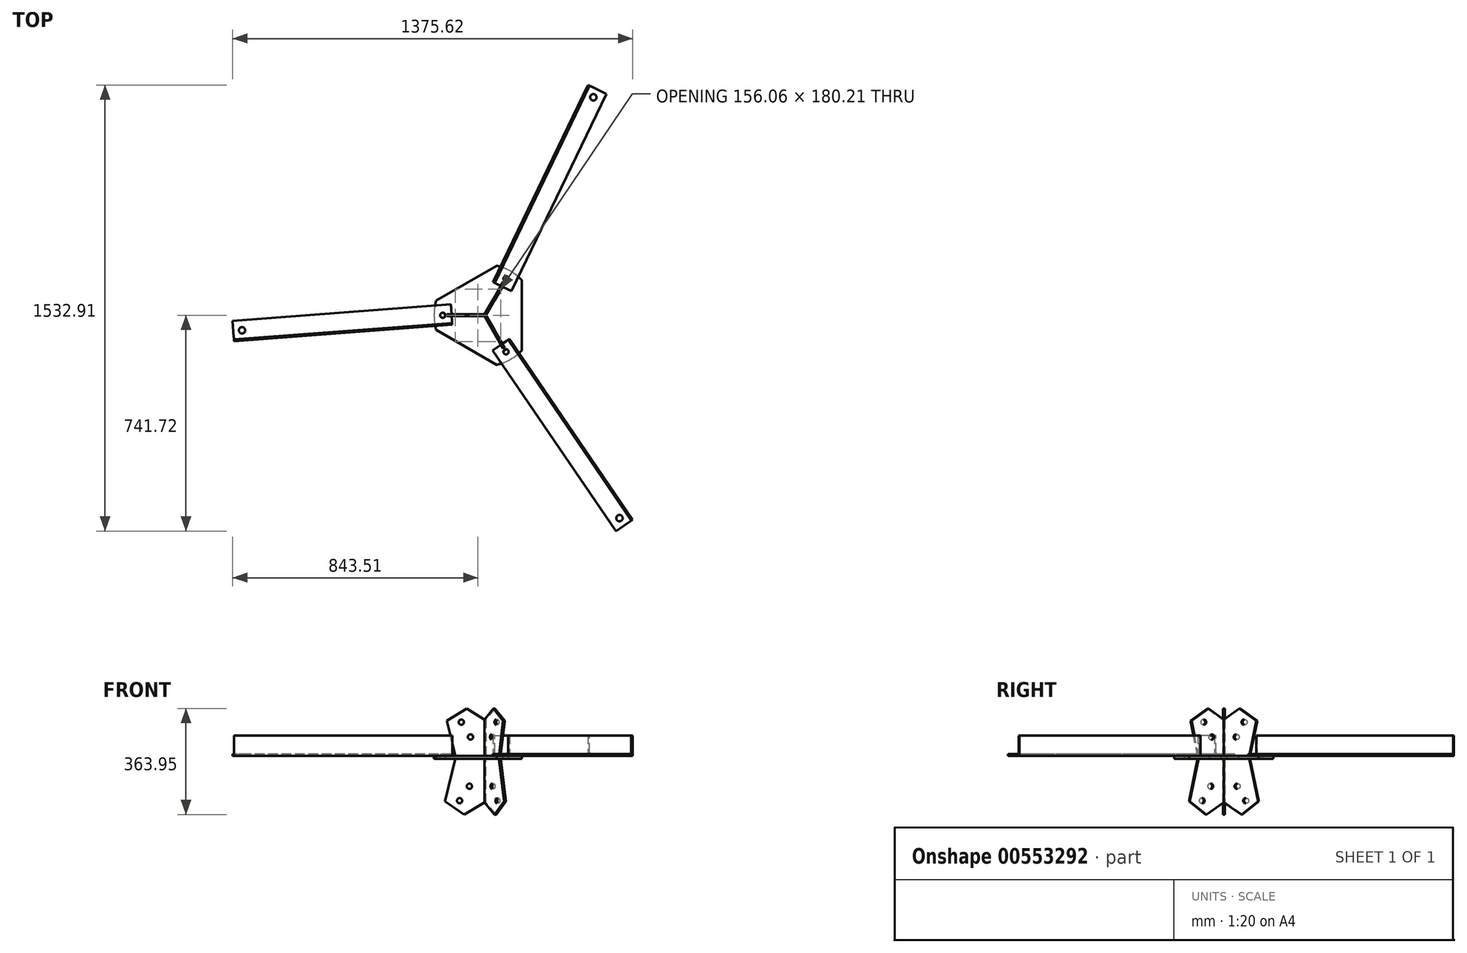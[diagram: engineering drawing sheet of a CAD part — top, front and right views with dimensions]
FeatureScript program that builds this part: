
annotation { "Feature Type Name" : "Feature", "Feature Type Description" : "" }
export const myFeature = defineFeature(function(context is Context, id is Id, definition is map)
    precondition{}
    {
        {
            var Q0;
            Q0=qCreatedBy(makeId("Top.planeOp"),FACE);
            var sketch = newSketch(context, id + "F0", { "sketchPlane" : qUnion([Q0])});
            skArc(sketch, "E0", {"start": v(40.55, -170.24) * mm, "mid": v(87.5, -151.55) * mm, "end": v(127.15, -120.24) * mm});
            skLineSegment(sketch, "E1", {"start": v(40.55, -170.24) * mm, "end": v(-167.7, -50) * mm});
            skLineSegment(sketch, "E2", {"start": v(0, 0) * mm, "end": v(-248.61, 0) * mm, "construction": true});
            skLineSegment(sketch, "E3.MirrorCS", {"start": v(40.55, 170.24) * mm, "end": v(-167.7, 50) * mm});
            skLineSegment(sketch, "E4", {"start": v(0, 0) * mm, "end": v(113.61, -196.78) * mm, "construction": true});
            skLineSegment(sketch, "E5.MirrorCS", {"start": v(127.15, -120.24) * mm, "end": v(127.15, 120.24) * mm});
            skArc(sketch, "E6.trimOffspring", {"start": v(-167.7, 50) * mm, "mid": v(-175, 0) * mm, "end": v(-167.7, -50) * mm});
            skArc(sketch, "E7.trimOffspring", {"start": v(127.15, 120.24) * mm, "mid": v(87.5, 151.55) * mm, "end": v(40.55, 170.24) * mm});
            skSolve(sketch);
        }
        {
            var Q0;
            Q0=makeQuery(id+"F0.imprint","IMPRINT",FACE,{"disambiguationData":[TD([[makeQuery(id+"F0.imprint","IMPRINT",EDGE,{"derivedFrom":sQuery(id+"F0.wireOp",EDGE,"E0")}),1.0]])]});
            extrude(context, id + "F1", {"entities" : qUnion([Q0]), "depth" : 10 * mm, "offsetDistance" : 25 * mm});
        }
        {
            var Q0;
            Q0=makeQuery(id+"F1.opExtrude","CAP_FACE",FACE,{"disambiguationData":[OSD([sQuery(id+"F0.wireOp",EDGE,"E0"),sQuery(id+"F0.wireOp",EDGE,"oJbW3ULZ-2pRP-CatU-Atqn-FDPEkCRfx0l3")])],"isStart":false});
            var sketch = newSketch(context, id + "F2", { "sketchPlane" : qUnion([Q0])});
            skCircle(sketch, "E8", {"center": v(-145, 0) * mm, "radius": 9 * mm});
            skCircle(sketch, "E9", {"center": v(72.5, -125.57) * mm, "radius": 9 * mm});
            skCircle(sketch, "E10", {"center": v(72.5, 125.57) * mm, "radius": 9 * mm});
            skCircle(sketch, "E11", {"center": v(0, 0) * mm, "radius": 145 * mm, "construction": true});
            skLineSegment(sketch, "E12", {"start": v(72.5, 125.57) * mm, "end": v(0, 0) * mm});
            skLineSegment(sketch, "E13", {"start": v(0, 0) * mm, "end": v(-145, 0) * mm});
            skLineSegment(sketch, "E14", {"start": v(0, 0) * mm, "end": v(72.5, -125.57) * mm});
            skSolve(sketch);
        }
        {
            var Q0;
            Q0 = qSketchRegion(id + "F2", true);
            extrude(context, id + "F3", {"entities" : qUnion([Q0]), "operationType" : NewBodyOperationType.REMOVE, "oppositeDirection" : true, "depth" : 25 * mm, "offsetDistance" : 25 * mm});
        }
        {
            var Q0;
            Q0=makeQuery(id+"F1.opExtrude","CAP_FACE",FACE,{"disambiguationData":[OSD([sQuery(id+"F0.wireOp",EDGE,"E0")])],"isStart":false});
            var sketch = newSketch(context, id + "F4", { "sketchPlane" : qUnion([Q0])});
            skLineSegment(sketch, "E15", {"start": v(0, 0) * mm, "end": v(72.5, -125.57) * mm, "construction": true});
            skLineSegment(sketch, "E16", {"start": v(0, 0) * mm, "end": v(-145, 0) * mm, "construction": true});
            skLineSegment(sketch, "E17", {"start": v(0, 0) * mm, "end": v(72.5, 125.57) * mm, "construction": true});
            skLineSegment(sketch, "E18.0", {"start": v(-2.02, 3.5) * mm, "end": v(-74.92, 3.5) * mm});
            skLineSegment(sketch, "E18.1", {"start": v(-2.02, 3.5) * mm, "end": v(34.43, 66.63) * mm});
            skLineSegment(sketch, "E19.0", {"start": v(-2.02, -3.5) * mm, "end": v(-74.92, -3.5) * mm});
            skLineSegment(sketch, "E19.1", {"start": v(-2.02, -3.5) * mm, "end": v(34.47, -66.7) * mm});
            skLineSegment(sketch, "E20.0", {"start": v(4.04, 0) * mm, "end": v(40.53, -63.2) * mm});
            skLineSegment(sketch, "E20.1", {"start": v(4.04, 0) * mm, "end": v(40.5, 63.13) * mm});
            skLineSegment(sketch, "E21", {"start": v(40.53, -63.2) * mm, "end": v(34.47, -66.7) * mm});
            skLineSegment(sketch, "E22", {"start": v(40.5, 63.13) * mm, "end": v(34.43, 66.63) * mm});
            skCircle(sketch, "E23", {"center": v(0, 0) * mm, "radius": 75 * mm, "construction": true});
            skLineSegment(sketch, "E24", {"start": v(-74.92, -3.5) * mm, "end": v(-74.92, 3.5) * mm});
            skSolve(sketch);
        }
        {
            var Q0;
            Q0=qCreatedBy(makeId("Front.planeOp"),FACE);
            var sketch = newSketch(context, id + "F5", { "sketchPlane" : qUnion([Q0])});
            skLineSegment(sketch, "E25.trimOffspring", {"start": v(0, -16) * mm, "end": v(-925, -1374.5) * mm, "construction": true});
            skLineSegment(sketch, "E26", {"start": v(0, 0) * mm, "end": v(0, -32) * mm, "construction": true});
            skLineSegment(sketch, "E27", {"start": v(0, -16) * mm, "end": v(-196.24, -16) * mm, "construction": true});
            skLineSegment(sketch, "E28", {"start": v(-133.05, -149.22) * mm, "end": v(-65.51, -50.03) * mm, "construction": true});
            skLineSegment(sketch, "E29", {"start": v(-65.51, -50.03) * mm, "end": v(-7.65, -89.43) * mm, "construction": true});
            skLineSegment(sketch, "E30", {"start": v(-7.65, -89.43) * mm, "end": v(-75.2, -188.62) * mm, "construction": true});
            skCircle(sketch, "E31", {"center": v(-53.47, -94.53) * mm, "radius": 9 * mm});
            skCircle(sketch, "E32", {"center": v(-87.24, -144.12) * mm, "radius": 9 * mm});
            skLineSegment(sketch, "E33", {"start": v(-133.05, -149.22) * mm, "end": v(-75.2, -188.62) * mm, "construction": true});
            skLineSegment(sketch, "E34", {"start": v(-2.02, 0) * mm, "end": v(-102.02, 0) * mm});
            skLineSegment(sketch, "E35", {"start": v(-102.02, 0) * mm, "end": v(-137.18, -146.4) * mm});
            skLineSegment(sketch, "E36", {"start": v(-137.18, -146.4) * mm, "end": v(-71.06, -191.43) * mm});
            skLineSegment(sketch, "E37", {"start": v(-71.06, -191.43) * mm, "end": v(-2.02, -150) * mm});
            skLineSegment(sketch, "E38", {"start": v(-2.02, -150) * mm, "end": v(-2.02, 0) * mm});
            skSolve(sketch);
        }
        {
            var Q0;
            Q0 = qSketchRegion(id + "F5", true);
            extrude(context, id + "F6", {"entities" : qUnion([Q0]), "depth" : 7 * mm, "offsetDistance" : 25 * mm, "symmetric" : true});
        }
        {
            var Q0;
            Q0=makeQuery(id+"F6.opExtrude","SWEPT_BODY",BODY,{"disambiguationData":[OSD([sQuery(id+"F5.wireOp",EDGE,"E31"),sQuery(id+"F5.wireOp",EDGE,"E32"),sQuery(id+"F5.wireOp",EDGE,"E34"),sQuery(id+"F5.wireOp",EDGE,"E35"),sQuery(id+"F5.wireOp",EDGE,"E36"),sQuery(id+"F5.wireOp",EDGE,"E37"),sQuery(id+"F5.wireOp",EDGE,"E38")])]});
            var Q1;
            Q1=sQuery(id+"F4.wireOp",EDGE,"E23");
            circularPattern(context, id + "F7", {"entities" : qUnion([Q0]), "axis" : qUnion([Q1]), "angle" : 360 * degree, "instanceCount" : 3, "equalSpace" : true, "computeTransformsWithoutBuiltin" : true});
        }
        {
            var Q0;
            Q0=makeQuery(id+"F4.imprint","IMPRINT",FACE,{"disambiguationData":[TD([[makeQuery(id+"F4.imprint","IMPRINT",EDGE,{"derivedFrom":sQuery(id+"F4.wireOp",EDGE,"E18.0")}),1.0]])]});
            var sketch = newSketch(context, id + "F8", { "sketchPlane" : qUnion([Q0])});
            skLineSegment(sketch, "E39", {"start": v(-2.02, 3.5) * mm, "end": v(4.04, 0) * mm});
            skLineSegment(sketch, "E40", {"start": v(4.04, 0) * mm, "end": v(-2.02, -3.5) * mm});
            skLineSegment(sketch, "E41", {"start": v(-2.02, -3.5) * mm, "end": v(-2.02, 3.5) * mm});
            skSolve(sketch);
        }
        {
            var Q0;
            Q0 = qSketchRegion(id + "F8", true);
            var Q1;
            Q1=makeQuery(id+"F6.opExtrude","CAP_VERTEX",VERTEX,{"disambiguationData":[OSD([sQuery(id+"F5.wireOp",EDGE,"E37"),sQuery(id+"F5.wireOp",EDGE,"E38")])],"isStart":true});
            extrude(context, id + "F9", {"entities" : qUnion([Q0]), "operationType" : NewBodyOperationType.ADD, "endBound" : BoundingType.UP_TO_VERTEX, "oppositeDirection" : true, "depth" : 200 * mm, "endBoundEntityVertex" : qUnion([Q1]), "offsetDistance" : 25 * mm});
        }
        {
            var Q0;
            Q0=makeQuery(id+"F2.imprint","IMPRINT",FACE,{"disambiguationData":[TD([[makeQuery(id+"F2.imprint","IMPRINT",EDGE,{"derivedFrom":sQuery(id+"F2.wireOp",EDGE,"E8")}),-1.0]])]});
            var sketch = newSketch(context, id + "F10", { "sketchPlane" : qUnion([Q0])});
            skLineSegment(sketch, "E42", {"start": v(-115.08, 2.24) * mm, "end": v(-864.88, -54) * mm});
            skLineSegment(sketch, "E43", {"start": v(-145, 0) * mm, "end": v(-838.84, 0) * mm, "construction": true});
            skLineSegment(sketch, "E44", {"start": v(-838.84, 0) * mm, "end": v(-838.84, 0) * mm});
            skLineSegment(sketch, "E45", {"start": v(-838.84, 0) * mm, "end": v(-834.96, -51.75) * mm, "construction": true});
            skSolve(sketch);
        }
        {
            var Q0;
            Q0=sQuery(id+"F10.wireOp",VERTEX,"E42.start");
            var Q1;
            Q1=sQuery(id+"F10.wireOp",EDGE,"E42");
            cPlane(context, id + "F11", {"entities" : qUnion([Q0, Q1]), "cplaneType" : CPlaneType.LINE_POINT, "offset" : 25 * mm, "width" : 150 * mm, "height" : 150 * mm});
        }
        {
            var Q0;
            Q0=qCreatedBy(id+"F11.planeOp",FACE);
            var sketch = newSketch(context, id + "F12", { "sketchPlane" : qUnion([Q0])});
            skLineSegment(sketch, "E46", {"start": v(24.15, 10) * mm, "end": v(-45.85, 10) * mm});
            skLineSegment(sketch, "E47", {"start": v(-45.85, 10) * mm, "end": v(-45.85, 16) * mm});
            skLineSegment(sketch, "E48", {"start": v(-45.85, 16) * mm, "end": v(10.15, 16) * mm});
            skLineSegment(sketch, "E49", {"start": v(18.15, 24) * mm, "end": v(18.15, 80) * mm});
            skLineSegment(sketch, "E50", {"start": v(18.15, 80) * mm, "end": v(24.15, 80) * mm});
            skLineSegment(sketch, "E51", {"start": v(24.15, 80) * mm, "end": v(24.15, 10) * mm});
            skPoint(sketch, "E52.visualSharp", {"position": v(18.15, 16) * mm});
            skArc(sketch, "E52.filletArc", {"start": v(10.15, 16) * mm, "mid": v(15.81, 18.34) * mm, "end": v(18.15, 24) * mm});
            skSolve(sketch);
        }
        {
            var Q0;
            Q0 = qSketchRegion(id + "F12", true);
            var Q1;
            Q1=sQuery(id+"F10.wireOp",EDGE,"E42");
            sweep(context, id + "F13", {"profiles" : qUnion([Q0]), "path" : qUnion([Q1])});
        }
        {
            var Q0;
            Q0=makeQuery(id+"F13.opSweep","SWEPT_FACE",FACE,{"disambiguationData":[OSD([sQuery(id+"F10.wireOp",EDGE,"E42"),sQuery(id+"F12.wireOp",EDGE,"E48")])]});
            var sketch = newSketch(context, id + "F14", { "sketchPlane" : qUnion([Q0])});
            skCircle(sketch, "E53.0", {"center": v(-145, 0) * mm, "radius": 9 * mm});
            skLineSegment(sketch, "E54", {"start": v(-492.6, 9.02) * mm, "end": v(-492.64, 9.59) * mm, "construction": true});
            skCircle(sketch, "E55.MirrorC", {"center": v(-834.96, -51.75) * mm, "radius": 9 * mm, "construction": true});
            skCircle(sketch, "E56", {"center": v(-834.96, -51.75) * mm, "radius": 11 * mm});
            skSolve(sketch);
        }
        {
            var Q0;
            Q0=sQuery(id+"F14.wireOp",VERTEX,"E53.0.center");
            var Q1;
            Q1=makeQuery(id+"F13.opSweep","SWEPT_BODY",BODY,{"disambiguationData":[OSD([sQuery(id+"F10.wireOp",EDGE,"E42"),sQuery(id+"F12.wireOp",EDGE,"E46"),sQuery(id+"F12.wireOp",EDGE,"E47"),sQuery(id+"F12.wireOp",EDGE,"E48"),sQuery(id+"F12.wireOp",EDGE,"E49"),sQuery(id+"F12.wireOp",EDGE,"E50"),sQuery(id+"F12.wireOp",EDGE,"E51"),sQuery(id+"F12.wireOp",EDGE,"E52.filletArc")])]});
            hole(context, id + "F15", {"style" : HoleStyle.SIMPLE, "endStyle" : HoleEndStyle.BLIND, "holeDiameter" : 18 * mm, "majorDiameter" : 5 * mm, "holeDepth" : 22 * mm, "isTappedThrough" : true, "tappedDepth" : 12 * mm, "tapClearance" : 3, "locations" : qUnion([Q0]), "scope" : qUnion([Q1]), "startStyle" : HoleStartStyle.PART});
        }
        {
            var Q0;
            Q0=sQuery(id+"F10.wireOp",VERTEX,"E45.end");
            var Q1;
            Q1=makeQuery(id+"F13.opSweep","SWEPT_BODY",BODY,{"disambiguationData":[OSD([sQuery(id+"F10.wireOp",EDGE,"E42"),sQuery(id+"F12.wireOp",EDGE,"E46"),sQuery(id+"F12.wireOp",EDGE,"E47"),sQuery(id+"F12.wireOp",EDGE,"E48"),sQuery(id+"F12.wireOp",EDGE,"E49"),sQuery(id+"F12.wireOp",EDGE,"E50"),sQuery(id+"F12.wireOp",EDGE,"E51"),sQuery(id+"F12.wireOp",EDGE,"E52.filletArc")])]});
            hole(context, id + "F16", {"style" : HoleStyle.SIMPLE, "endStyle" : HoleEndStyle.BLIND, "oppositeDirection" : true, "holeDiameter" : 22 * mm, "majorDiameter" : 5 * mm, "holeDepth" : 22 * mm, "isTappedThrough" : true, "tappedDepth" : 12 * mm, "tapClearance" : 3, "locations" : qUnion([Q0]), "scope" : qUnion([Q1]), "startStyle" : HoleStartStyle.PART});
        }
        {
            var Q0;
            Q0=makeQuery(id+"F13.opSweep","SWEPT_BODY",BODY,{"disambiguationData":[OSD([sQuery(id+"F10.wireOp",EDGE,"E42"),sQuery(id+"F12.wireOp",EDGE,"E46"),sQuery(id+"F12.wireOp",EDGE,"E47"),sQuery(id+"F12.wireOp",EDGE,"E48"),sQuery(id+"F12.wireOp",EDGE,"E49"),sQuery(id+"F12.wireOp",EDGE,"E50"),sQuery(id+"F12.wireOp",EDGE,"E51"),sQuery(id+"F12.wireOp",EDGE,"E52.filletArc")])]});
            var Q1;
            Q1=sQuery(id+"F4.wireOp",EDGE,"E23");
            circularPattern(context, id + "F17", {"entities" : qUnion([Q0]), "axis" : qUnion([Q1]), "angle" : 360 * degree, "instanceCount" : 3, "equalSpace" : true, "computeTransformsWithoutBuiltin" : true});
        }
        {
            var Q0;
            Q0=qCreatedBy(makeId("Front.planeOp"),FACE);
            var sketch = newSketch(context, id + "F18", { "sketchPlane" : qUnion([Q0])});
            skLineSegment(sketch, "E57", {"start": v(-2.02, 10) * mm, "end": v(-102.02, 10) * mm});
            skLineSegment(sketch, "E58", {"start": v(-102.02, 10) * mm, "end": v(-130.9, 130.66) * mm});
            skLineSegment(sketch, "E59", {"start": v(-130.9, 130.66) * mm, "end": v(-62.74, 172.52) * mm});
            skLineSegment(sketch, "E60", {"start": v(-62.74, 172.52) * mm, "end": v(-2.02, 135) * mm});
            skLineSegment(sketch, "E61", {"start": v(-2.02, 135) * mm, "end": v(-2.02, 10) * mm});
            skLineSegment(sketch, "E62", {"start": v(-3.72, 0) * mm, "end": v(-925, 1500) * mm, "construction": true});
            skLineSegment(sketch, "E63", {"start": v(-126.65, 133.27) * mm, "end": v(-63.85, 31.02) * mm, "construction": true});
            skLineSegment(sketch, "E64", {"start": v(-63.85, 31.02) * mm, "end": v(-4.2, 67.65) * mm, "construction": true});
            skLineSegment(sketch, "E65", {"start": v(-4.2, 67.65) * mm, "end": v(-67, 169.9) * mm, "construction": true});
            skLineSegment(sketch, "E66", {"start": v(-67, 169.9) * mm, "end": v(-126.65, 133.27) * mm, "construction": true});
            skCircle(sketch, "E67", {"center": v(-49.72, 74.9) * mm, "radius": 9 * mm});
            skCircle(sketch, "E68", {"center": v(-81.12, 126.03) * mm, "radius": 9 * mm});
            skSolve(sketch);
        }
        {
            var Q0;
            Q0 = qSketchRegion(id + "F18", true);
            extrude(context, id + "F19", {"entities" : qUnion([Q0]), "depth" : 7 * mm, "offsetDistance" : 25 * mm, "symmetric" : true});
        }
        {
            var Q0;
            Q0=makeQuery(id+"F19.opExtrude","SWEPT_BODY",BODY,{"disambiguationData":[OSD([sQuery(id+"F18.wireOp",EDGE,"E57"),sQuery(id+"F18.wireOp",EDGE,"E58"),sQuery(id+"F18.wireOp",EDGE,"E59"),sQuery(id+"F18.wireOp",EDGE,"E60"),sQuery(id+"F18.wireOp",EDGE,"E61"),sQuery(id+"F18.wireOp",EDGE,"E67"),sQuery(id+"F18.wireOp",EDGE,"E68")])]});
            var Q1;
            Q1=sQuery(id+"F4.wireOp",EDGE,"E23");
            circularPattern(context, id + "F20", {"entities" : qUnion([Q0]), "axis" : qUnion([Q1]), "angle" : 360 * degree, "instanceCount" : 3, "equalSpace" : true, "computeTransformsWithoutBuiltin" : true});
        }
        {
            var Q0;
            Q0=makeQuery(id+"F10.imprint","IMPRINT",FACE,{"disambiguationData":[TD([[makeQuery(id+"F10.imprint","IMPRINT",EDGE,{"derivedFrom":makeQuery(id+"F2.imprint","IMPRINT",EDGE,{"derivedFrom":sQuery(id+"F2.wireOp",EDGE,"E9")})}),-1.0]])]});
            var sketch = newSketch(context, id + "F21", { "sketchPlane" : qUnion([Q0])});
            skLineSegment(sketch, "E69.0", {"start": v(4.04, 0) * mm, "end": v(-2.02, -3.5) * mm});
            skLineSegment(sketch, "E69.1", {"start": v(-2.02, -3.5) * mm, "end": v(-2.02, 3.5) * mm});
            skLineSegment(sketch, "E69.2", {"start": v(-2.02, 3.5) * mm, "end": v(4.04, 0) * mm});
            skSolve(sketch);
        }
        {
            var Q0;
            Q0 = qSketchRegion(id + "F21", true);
            var Q1;
            Q1=makeQuery(id+"F20.opPattern","COPY",VERTEX,{"derivedFrom":makeQuery(id+"F19.opExtrude","CAP_VERTEX",VERTEX,{"disambiguationData":[OSD([sQuery(id+"F18.wireOp",EDGE,"E60"),sQuery(id+"F18.wireOp",EDGE,"E61")])],"isStart":true}),"instanceName":"2"});
            extrude(context, id + "F22", {"entities" : qUnion([Q0]), "operationType" : NewBodyOperationType.ADD, "endBound" : BoundingType.UP_TO_VERTEX, "depth" : 25 * mm, "endBoundEntityVertex" : qUnion([Q1]), "offsetDistance" : 25 * mm});
        }
    });
